# Revit family: TAG1
name_source: partatom
category: Furniture
units: mm (PartAtom-declared; Revit-internal decimal feet)

## family parameters
Always vertical = Yes
Cut with Voids When Loaded = No
OmniClass Number = 23.40.20.00
OmniClass Title = General Furniture and Specialties
Render Appearance Source = Family Geometry
Room Calculation Point = No
Shared = No
Work Plane-Based = No

## types (1)
- CW009
    Default Elevation = 0 mm  [stored 0 ft]
    Description = 6 x CaseWorks L-Bracket (Single) 5.5Hx1Wx1D, 1 x CaseWorks Countertop Laminate 24Dx72W, 1 x CaseWorks Countertop Laminate 24Dx86W, 1 x CaseWorks Countertop Laminate 24Dx90W, 1 x CaseWorks Base Cabinet Side Filler 28_5HxWx6D (Cut to size on-site), 2 x CaseWorks Wall Cabinet Side Filler 30HxWx6D (Cut to size on-site), 1 x CaseWorks Sink Faucet Stainless Single Handle w/Side Spray, 1 x CaseWorks Sink Faucet Hole Cover, 1 x CaseWorks Sink Stainless Steel 8-1/16Hx25Wx22L (Std) Drop In, 1 x CaseWorks Toe Kick 04Hx59W (Cut to size on-site), 1 x CaseWorks Toe Kick 04Hx61W (Cut to size on-site), 1 x CaseWorks Toe Kick 04Hx90W (Cut to size on-site), 1 x CaseWorks Side Toe Kick 04Hx20.22W (Cut to size on-site), 1 x CaseWorks Base Cab Double Doors Single Drawer 33Hx36Wx24D, 1 x CaseWorks Base Corner Cabinet Single Door Right 33Hx36Wx24D, 1 x CaseWorks Base Cabinet Single Door Right 33Hx18Wx24D, 1 x CaseWorks Base Appliance Garage Cabinet 33Hx30Wx24D, 1 x CaseWorks Base Cabinet Four Drawers 33Hx36Wx24D, 1 x CaseWorks Base Cabinet Open 33Hx18Wx24D, 1 x CaseWorks Base Sink Cabinet Double Doors 33Hx36Wx24D, 1 x CaseWorks Base Cabinet Trash Pullout 33Hx24Wx24D, 1 x CaseWorks Wood Wall Cleat - 72" (Cut to size on-site), 1 x CaseWorks Wood Wall Cleat - 96" (Cut to size on-site), 1 x CaseWorks Wall Cabinet Single Door Left 30Hx18Wx15D, 2 x CaseWorks Wall Cabinet Double Door 30Hx36Wx15D, 1 x CaseWorks Wall Cabinet L Shelves 30Hx36Wx15D, 1 x CaseWorks Wall Cabinet Microwave 30Hx34Wx15D, 2 x 86 Degree Hinge Restriction Clip, 13 x Soft Close Mechanism for Hinged Doors
    Exported From CET Designer = Yes
    Manufacturer = AIS
    Model = M-ACB
    Show CW009 = Yes
    VisibilityIndex = 0

note: [stored X ft] marks values corroborated as IEEE doubles in the binary element streams (Revit-internal decimal feet)

## geometry (parser evidence)
native form markers: Sweep x3
no freeform markers — native parametric forms only
